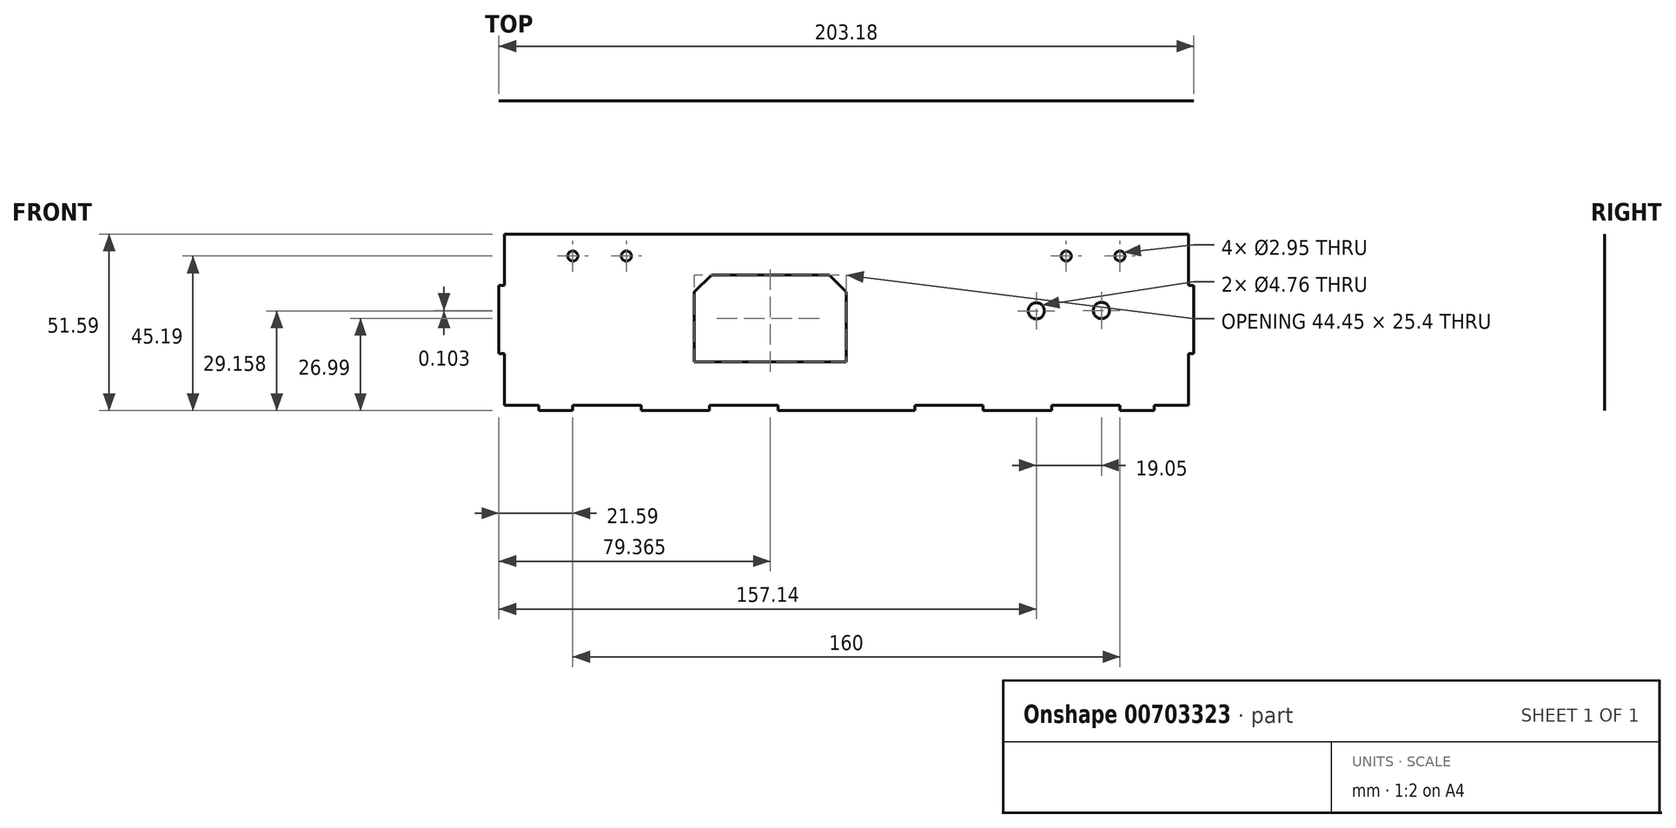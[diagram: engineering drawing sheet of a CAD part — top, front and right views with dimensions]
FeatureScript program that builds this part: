
annotation { "Feature Type Name" : "Feature", "Feature Type Description" : "" }
export const myFeature = defineFeature(function(context is Context, id is Id, definition is map)
    precondition{}
    {
        {
            var Q0;
            Q0=qCreatedBy(makeId("Front.planeOp"),FACE);
            var sketch = newSketch(context, id + "F0", { "sketchPlane" : qUnion([Q0])});
            skLineSegment(sketch, "E0.bottom", {"start": v(100, 25) * mm, "end": v(-100, 25) * mm});
            skLineSegment(sketch, "E0.top", {"start": v(100, -25) * mm, "end": v(-100, -25) * mm});
            skLineSegment(sketch, "E0.left", {"start": v(100, 25) * mm, "end": v(100, -25) * mm});
            skLineSegment(sketch, "E0.right", {"start": v(-100, 25) * mm, "end": v(-100, -25) * mm});
            skPoint(sketch, "E0.middle", {"position": v(0, 0) * mm});
            skLineSegment(sketch, "E1", {"start": v(90, -25) * mm, "end": v(90, -26.59) * mm});
            skLineSegment(sketch, "E2", {"start": v(90, -26.59) * mm, "end": v(80, -26.59) * mm});
            skLineSegment(sketch, "E3", {"start": v(80, -26.59) * mm, "end": v(80, -25) * mm});
            skLineSegment(sketch, "E4", {"start": v(-90, -25) * mm, "end": v(-90, -26.59) * mm});
            skLineSegment(sketch, "E5", {"start": v(-90, -26.59) * mm, "end": v(-80, -26.59) * mm});
            skLineSegment(sketch, "E6", {"start": v(-80, -26.59) * mm, "end": v(-80, -25) * mm});
            skLineSegment(sketch, "E7", {"start": v(-60, -25) * mm, "end": v(-60, -26.59) * mm});
            skLineSegment(sketch, "E8", {"start": v(-60, -26.59) * mm, "end": v(-40, -26.59) * mm});
            skLineSegment(sketch, "E9", {"start": v(-40, -26.59) * mm, "end": v(-40, -25) * mm});
            skLineSegment(sketch, "E10", {"start": v(-20, -25) * mm, "end": v(-20, -26.59) * mm});
            skLineSegment(sketch, "E11", {"start": v(-20, -26.59) * mm, "end": v(20, -26.59) * mm});
            skLineSegment(sketch, "E12", {"start": v(20, -26.59) * mm, "end": v(20, -25) * mm});
            skLineSegment(sketch, "E13", {"start": v(60, -25) * mm, "end": v(60, -26.59) * mm});
            skLineSegment(sketch, "E14", {"start": v(60, -26.59) * mm, "end": v(40, -26.59) * mm});
            skLineSegment(sketch, "E15", {"start": v(40, -26.59) * mm, "end": v(40, -25) * mm});
            skLineSegment(sketch, "E16", {"start": v(-100, -10) * mm, "end": v(-101.59, -10) * mm});
            skLineSegment(sketch, "E17", {"start": v(-101.59, -10) * mm, "end": v(-101.59, 10) * mm});
            skLineSegment(sketch, "E18", {"start": v(-101.59, 10) * mm, "end": v(-100, 10) * mm});
            skLineSegment(sketch, "E19", {"start": v(100, -10) * mm, "end": v(101.59, -10) * mm});
            skLineSegment(sketch, "E20", {"start": v(101.59, -10) * mm, "end": v(101.59, 10) * mm});
            skLineSegment(sketch, "E21", {"start": v(101.59, 10) * mm, "end": v(100, 10) * mm});
            skCircle(sketch, "E22", {"center": v(80, 18.6) * mm, "radius": 1.47 * mm});
            skCircle(sketch, "E23", {"center": v(64.3, 18.6) * mm, "radius": 1.47 * mm});
            skCircle(sketch, "E24", {"center": v(-80, 18.6) * mm, "radius": 1.47 * mm});
            skCircle(sketch, "E25", {"center": v(-64.3, 18.6) * mm, "radius": 1.47 * mm});
            skLineSegment(sketch, "E26", {"start": v(-44.45, -25) * mm, "end": v(-44.45, 13.1) * mm});
            skLineSegment(sketch, "E27", {"start": v(-44.45, 13.1) * mm, "end": v(0, 13.1) * mm});
            skLineSegment(sketch, "E28", {"start": v(0, 13.1) * mm, "end": v(0, -25) * mm});
            skLineSegment(sketch, "E29", {"start": v(-44.45, -12.3) * mm, "end": v(0, -12.3) * mm});
            skCircle(sketch, "E30", {"center": v(55.55, 2.57) * mm, "radius": 2.38 * mm});
            skCircle(sketch, "E31", {"center": v(74.6, 2.67) * mm, "radius": 2.38 * mm});
            skSolve(sketch);
        }
        {
            var Q0;
            Q0 = qSketchRegion(id + "F0", true);
            extrude(context, id + "F1", {"entities" : qUnion([Q0]), "depth" : 1 / 406.4 * mm, "offsetDistance" : 25 * mm});
        }
        {
            var Q0;
            Q0=makeQuery(id+"F1.opExtrude","SWEPT_EDGE",EDGE,{"disambiguationData":[OSD([sQuery(id+"F0.wireOp",EDGE,"E26"),sQuery(id+"F0.wireOp",EDGE,"E27")])]});
            var Q1;
            Q1=makeQuery(id+"F1.opExtrude","SWEPT_EDGE",EDGE,{"disambiguationData":[OSD([sQuery(id+"F0.wireOp",EDGE,"E27"),sQuery(id+"F0.wireOp",EDGE,"E28")])]});
            chamfer(context, id + "F2", {"entities" : qUnion([Q0, Q1]), "width" : 5 * mm, "tangentPropagation" : true});
        }
    });
